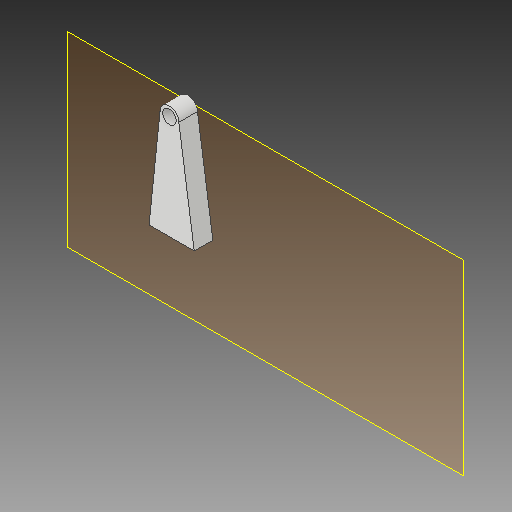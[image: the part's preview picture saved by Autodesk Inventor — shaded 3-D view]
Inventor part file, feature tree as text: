
AUTODESK INVENTOR PART (.ipt)
format: ipt  version: 2017 (Build 210142000, 142)  size: 86,528 bytes
history: native  units: in
note: dims shown in document units (in); Inventor stores cm internally (conversion verified against a paired STEP export)
features: other x5, plane x1, extrude x1, sketch x1, reference x1
ambient origin geometry x8: Origin, YZ Plane, XZ Plane, XY Plane, X Axis, Y Axis, Z Axis, Center Point
bodies: Solid1 (feature_tree)
feature tree (9):
  plane  "Work Plane1"
  extrude  "Extrusion1"  [1 undecoded]
  sketch  "Sketch1"  dims[d0=0.1181in d1=0.0in]
  reference  "Reference1"
  other  "<userpath>\ownCloud\pfc\projeto\asa1\assembly.iam"
  other  "assembly.iam"
  other  "WIRE:1"
  other  "<userpath>\Desktop\asa1\assembly.iam"
  other  "Part1:1"
note: 1 required parameter value undecoded (feature->parameter linkage not recoverable at this tier; creation-order binding heuristic only, values carry confidence <= 0.55)
